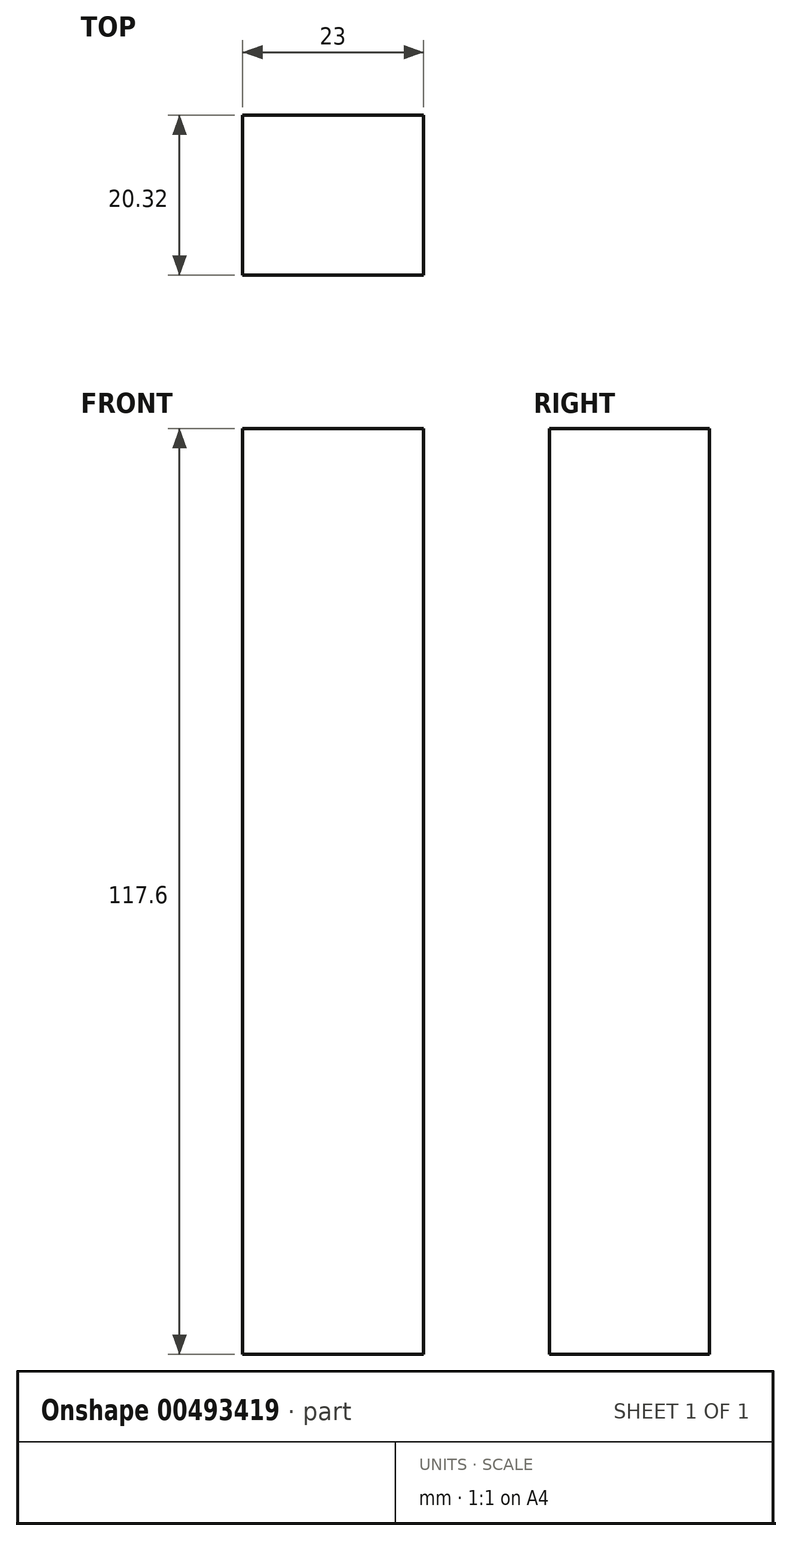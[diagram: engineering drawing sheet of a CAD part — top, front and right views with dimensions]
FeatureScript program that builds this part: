
annotation { "Feature Type Name" : "Feature", "Feature Type Description" : "" }
export const myFeature = defineFeature(function(context is Context, id is Id, definition is map)
    precondition{}
    {
        {
            var Q0;
            Q0=qCreatedBy(makeId("Front.planeOp"),FACE);
            var sketch = newSketch(context, id + "F0", { "sketchPlane" : qUnion([Q0])});
            skLineSegment(sketch, "E0.bottom", {"start": v(-10.48, 94.93) * mm, "end": v(12.52, 94.93) * mm});
            skLineSegment(sketch, "E0.top", {"start": v(-10.48, -22.67) * mm, "end": v(12.52, -22.67) * mm});
            skLineSegment(sketch, "E0.left", {"start": v(-10.48, 94.93) * mm, "end": v(-10.48, -22.67) * mm});
            skLineSegment(sketch, "E0.right", {"start": v(12.52, 94.93) * mm, "end": v(12.52, -22.67) * mm});
            skSolve(sketch);
        }
        {
            var Q0;
            Q0 = qConstructionFilter(qBodyType(qCreatedBy(id + "F0" ,EDGE), BodyType.WIRE), ConstructionObject.NO);
            extrude(context, id + "F1", {"bodyType" : ToolBodyType.SURFACE, "surfaceEntities" : qUnion([Q0]), "depth" : 20.32 * mm});
        }
    });
